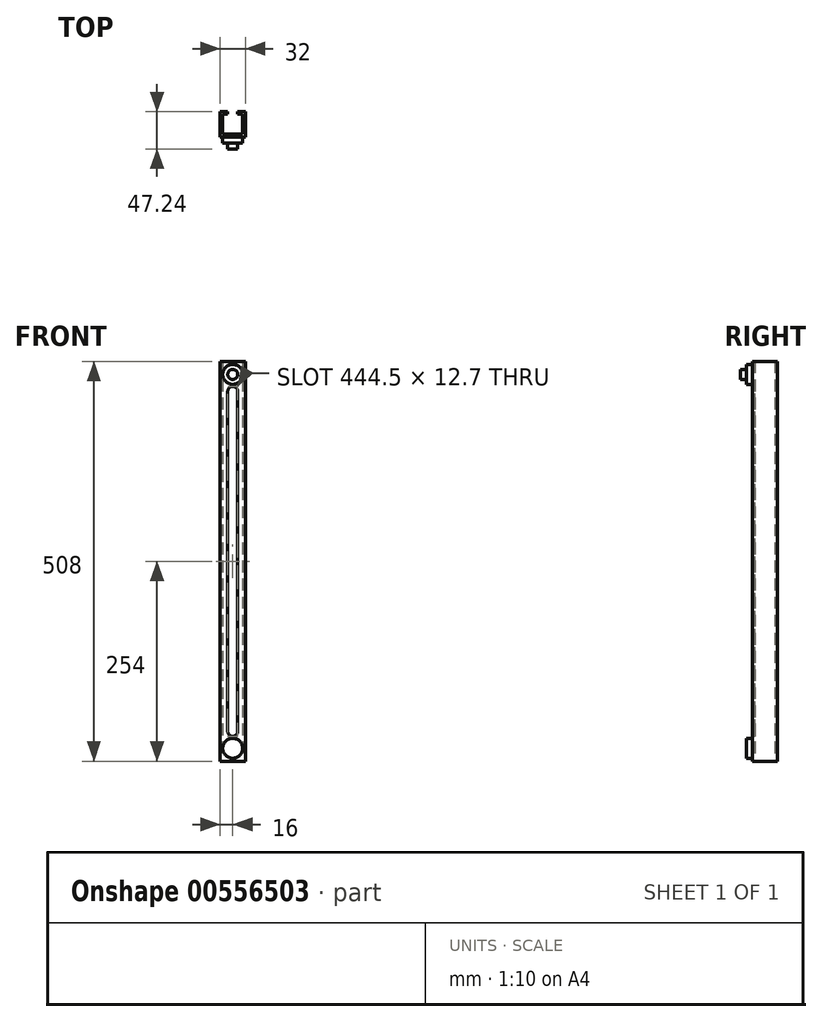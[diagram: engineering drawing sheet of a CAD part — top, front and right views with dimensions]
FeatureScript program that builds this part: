
annotation { "Feature Type Name" : "Feature", "Feature Type Description" : "" }
export const myFeature = defineFeature(function(context is Context, id is Id, definition is map)
    precondition{}
    {
        {
            var Q0;
            Q0=qCreatedBy(makeId("Top.planeOp"),FACE);
            var sketch = newSketch(context, id + "F0", { "sketchPlane" : qUnion([Q0])});
            skLineSegment(sketch, "E0", {"start": v(-16, 0) * mm, "end": v(-16, 32) * mm});
            skLineSegment(sketch, "E1", {"start": v(-16, 32) * mm, "end": v(-6.35, 32) * mm});
            skLineSegment(sketch, "E2", {"start": v(-6.35, 32) * mm, "end": v(-6.35, 28.7) * mm});
            skLineSegment(sketch, "E3", {"start": v(-6.35, 28.7) * mm, "end": v(-12.7, 28.7) * mm});
            skLineSegment(sketch, "E4", {"start": v(-12.7, 28.7) * mm, "end": v(-12.7, 3.3) * mm});
            skLineSegment(sketch, "E5", {"start": v(-12.7, 3.3) * mm, "end": v(0, 3.3) * mm});
            skLineSegment(sketch, "E6", {"start": v(0, 0) * mm, "end": v(-16, 0) * mm});
            skLineSegment(sketch, "E7.MirrorCS", {"start": v(6.35, 32) * mm, "end": v(6.35, 28.7) * mm});
            skLineSegment(sketch, "E8.MirrorCS", {"start": v(16, 0) * mm, "end": v(16, 32) * mm});
            skLineSegment(sketch, "E9.MirrorCS", {"start": v(0, 0) * mm, "end": v(16, 0) * mm});
            skLineSegment(sketch, "E10.MirrorCS", {"start": v(16, 32) * mm, "end": v(6.35, 32) * mm});
            skLineSegment(sketch, "E11.MirrorCS", {"start": v(6.35, 28.7) * mm, "end": v(12.7, 28.7) * mm});
            skLineSegment(sketch, "E12.MirrorCS", {"start": v(12.7, 3.3) * mm, "end": v(0, 3.3) * mm});
            skLineSegment(sketch, "E13.MirrorCS", {"start": v(12.7, 28.7) * mm, "end": v(12.7, 3.3) * mm});
            skSolve(sketch);
        }
        {
            var Q0;
            Q0 = qSketchRegion(id + "F0", true);
            extrude(context, id + "F1", {"entities" : qUnion([Q0]), "depth" : 508 * mm, "offsetDistance" : 25.4 * mm});
        }
        {
            var Q0;
            Q0=makeQuery(id+"F1.opExtrude","SWEPT_FACE",FACE,{"disambiguationData":[OSD([sQuery(id+"F0.wireOp",EDGE,"E6"),sQuery(id+"F0.wireOp",EDGE,"E9.MirrorCS")])]});
            var sketch = newSketch(context, id + "F2", { "sketchPlane" : qUnion([Q0])});
            skCircle(sketch, "E14", {"center": v(0, 491.5) * mm, "radius": 12.7 * mm});
            skCircle(sketch, "E15", {"center": v(0, 491.5) * mm, "radius": 6.35 * mm});
            skCircle(sketch, "E16", {"center": v(0, 16.51) * mm, "radius": 12.7 * mm});
            skSolve(sketch);
        }
        {
            var Q0;
            Q0 = qSketchRegion(id + "F2", true);
            extrude(context, id + "F3", {"entities" : qUnion([Q0]), "operationType" : NewBodyOperationType.ADD, "depth" : 7.62 * mm, "offsetDistance" : 25.4 * mm});
        }
        {
            var Q0;
            Q0=makeQuery(id+"F3.boolean.opBoolean","SPLIT",FACE,{"disambiguationData":[TD([makeQuery(id+"F3.opExtrude","SWEPT_FACE",FACE,{"disambiguationData":[OSD([sQuery(id+"F2.wireOp",EDGE,"E15")])]})])],"derivedFrom":makeQuery(id+"F1.opExtrude","SWEPT_FACE",FACE,{"disambiguationData":[OSD([sQuery(id+"F0.wireOp",EDGE,"E6"),sQuery(id+"F0.wireOp",EDGE,"E9.MirrorCS")])]})});
            extrude(context, id + "F4", {"entities" : qUnion([Q0]), "operationType" : NewBodyOperationType.ADD, "depth" : 15.24 * mm, "offsetDistance" : 25.4 * mm});
        }
        {
            var Q0;
            {var subQ4=sQuery(id+"F0.wireOp",EDGE,"E9.MirrorCS");var subQ7=sQuery(id+"F0.wireOp",EDGE,"E6");var subQ13=sQuery(id+"F0.wireOp",EDGE,"E0");Q0=makeQuery(id+"F3.boolean.opBoolean","SPLIT",FACE,{"disambiguationData":[TD([makeQuery(id+"F1.opExtrude","SWEPT_FACE",FACE,{"disambiguationData":[OSD([subQ13])]})])],"derivedFrom":makeQuery(id+"F1.opExtrude","SWEPT_FACE",FACE,{"disambiguationData":[OSD([subQ7,subQ4])]})});}
            var sketch = newSketch(context, id + "F5", { "sketchPlane" : qUnion([Q0])});
            skLineSegment(sketch, "E17", {"start": v(-6.35, 38.1) * mm, "end": v(-6.35, 469.9) * mm});
            skLineSegment(sketch, "E18", {"start": v(6.35, 469.9) * mm, "end": v(6.35, 38.1) * mm});
            skArc(sketch, "E19", {"start": v(6.35, 469.9) * mm, "mid": v(0, 476.25) * mm, "end": v(-6.35, 469.9) * mm});
            skArc(sketch, "E20", {"start": v(-6.35, 38.1) * mm, "mid": v(0, 31.75) * mm, "end": v(6.35, 38.1) * mm});
            skSolve(sketch);
        }
        {
            var Q0;
            Q0 = qSketchRegion(id + "F5", true);
            extrude(context, id + "F6", {"entities" : qUnion([Q0]), "operationType" : NewBodyOperationType.REMOVE, "endBound" : BoundingType.UP_TO_NEXT, "oppositeDirection" : true, "depth" : 25.4 * mm, "offsetDistance" : 25.4 * mm});
        }
    });
